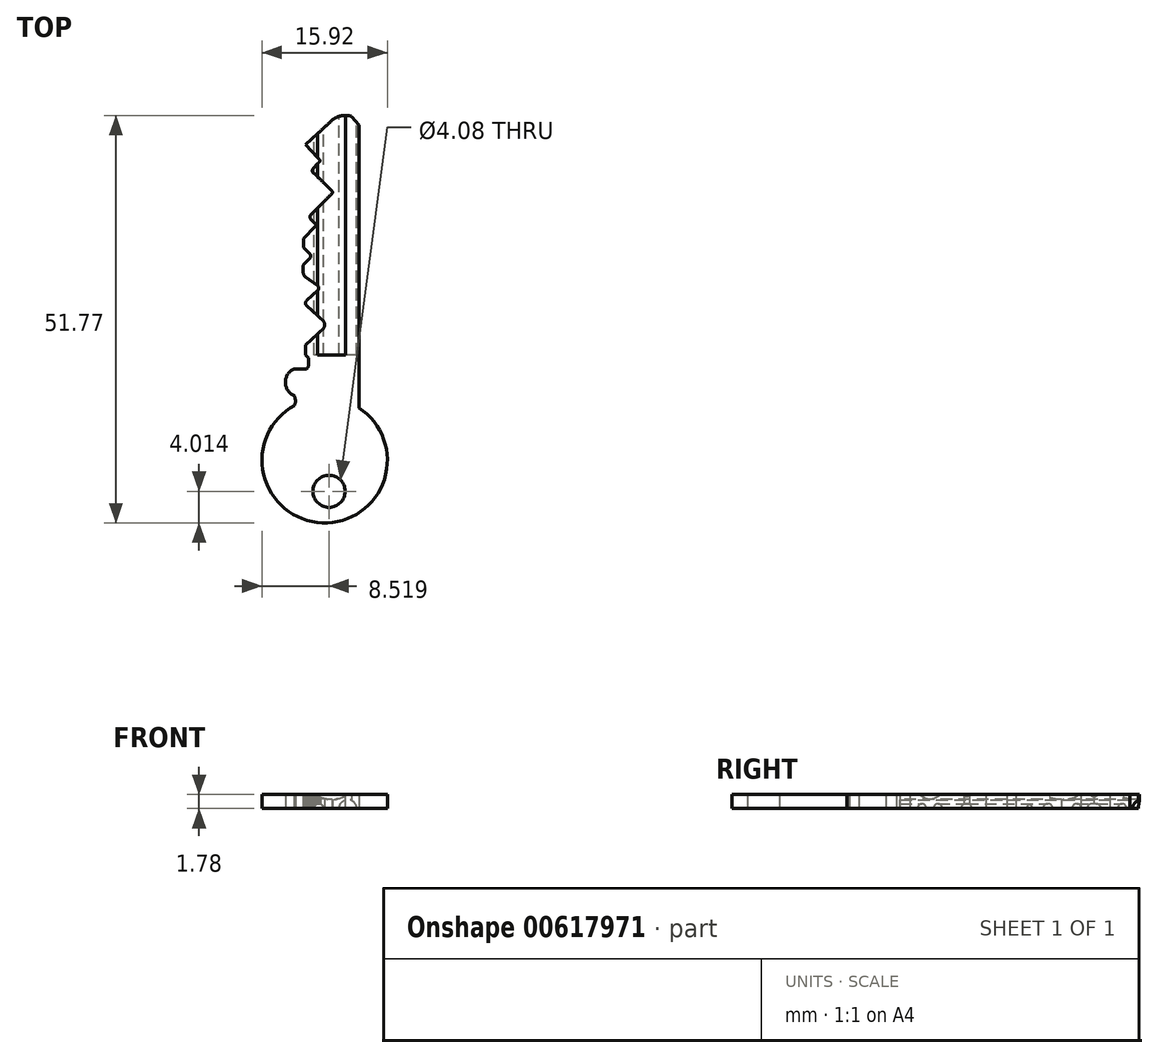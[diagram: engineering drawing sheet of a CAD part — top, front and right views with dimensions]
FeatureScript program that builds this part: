
annotation { "Feature Type Name" : "Feature", "Feature Type Description" : "" }
export const myFeature = defineFeature(function(context is Context, id is Id, definition is map)
    precondition{}
    {
        {
            var Q0;
            Q0=qCreatedBy(makeId("Top.planeOp"),FACE);
            var sketch = newSketch(context, id + "F0", { "sketchPlane" : qUnion([Q0])});
            skLineSegment(sketch, "E0", {"start": v(-2.25, 0) * mm, "end": v(-2.25, 27.94) * mm});
            skLineSegment(sketch, "E1", {"start": v(-2.25, 27.94) * mm, "end": v(-3.17, 29) * mm});
            skArc(sketch, "E2", {"start": v(-3.17, 29) * mm, "mid": v(-4.52, 29.1) * mm, "end": v(-5.72, 28.47) * mm});
            skPoint(sketch, "E2.endSnap0", {"position": v(-2.7, 28.47) * mm});
            skLineSegment(sketch, "E3", {"start": v(-5.72, 28.47) * mm, "end": v(-9.02, 25.42) * mm});
            skLineSegment(sketch, "E4", {"start": v(-9.02, 25.42) * mm, "end": v(-7.14, 23.39) * mm});
            skLineSegment(sketch, "E5", {"start": v(-7.14, 23.39) * mm, "end": v(-8.07, 22.39) * mm});
            skArc(sketch, "E6", {"start": v(-8.07, 22.39) * mm, "mid": v(-8.17, 22.02) * mm, "end": v(-7.92, 21.74) * mm});
            skLineSegment(sketch, "E7", {"start": v(-7.92, 21.74) * mm, "end": v(-5.67, 19.53) * mm});
            skArc(sketch, "E8", {"start": v(-5.67, 19.24) * mm, "mid": v(-5.6, 19.38) * mm, "end": v(-5.67, 19.53) * mm});
            skLineSegment(sketch, "E9", {"start": v(-5.67, 19.24) * mm, "end": v(-8.39, 16.47) * mm});
            skArc(sketch, "E10", {"start": v(-8.39, 16.47) * mm, "mid": v(-8.49, 16.23) * mm, "end": v(-8.39, 15.98) * mm});
            skLineSegment(sketch, "E11", {"start": v(-8.39, 15.98) * mm, "end": v(-7.8, 15.38) * mm});
            skArc(sketch, "E12", {"start": v(-7.8, 15) * mm, "mid": v(-7.72, 15.19) * mm, "end": v(-7.8, 15.38) * mm});
            skLineSegment(sketch, "E13", {"start": v(-7.8, 15) * mm, "end": v(-9.3, 13.47) * mm});
            skLineSegment(sketch, "E14", {"start": v(-9.3, 13.47) * mm, "end": v(-9.3, 12.33) * mm});
            skLineSegment(sketch, "E15", {"start": v(-9.3, 12.33) * mm, "end": v(-8.48, 11.53) * mm});
            skArc(sketch, "E16", {"start": v(-8.48, 10.99) * mm, "mid": v(-8.37, 11.26) * mm, "end": v(-8.48, 11.53) * mm});
            skLineSegment(sketch, "E17", {"start": v(-8.48, 10.99) * mm, "end": v(-9.19, 10.3) * mm});
            skArc(sketch, "E18", {"start": v(-9.19, 10.3) * mm, "mid": v(-9.36, 9.98) * mm, "end": v(-9.33, 9.63) * mm});
            skLineSegment(sketch, "E19", {"start": v(-9.33, 9.63) * mm, "end": v(-9.33, 9.19) * mm});
            skArc(sketch, "E20", {"start": v(-9.33, 9.19) * mm, "mid": v(-9.25, 8.86) * mm, "end": v(-9.02, 8.6) * mm});
            skLineSegment(sketch, "E21", {"start": v(-9.02, 8.6) * mm, "end": v(-7.53, 7.53) * mm});
            skArc(sketch, "E22", {"start": v(-7.53, 6.87) * mm, "mid": v(-7.35, 7.2) * mm, "end": v(-7.53, 7.53) * mm});
            skLineSegment(sketch, "E23", {"start": v(-7.53, 6.87) * mm, "end": v(-8.87, 5.67) * mm});
            skArc(sketch, "E24", {"start": v(-8.87, 5.67) * mm, "mid": v(-9.04, 5.3) * mm, "end": v(-8.87, 4.92) * mm});
            skLineSegment(sketch, "E25", {"start": v(-8.87, 4.92) * mm, "end": v(-6.89, 3.14) * mm});
            skArc(sketch, "E26", {"start": v(-6.89, 1.94) * mm, "mid": v(-6.62, 2.54) * mm, "end": v(-6.89, 3.14) * mm});
            skLineSegment(sketch, "E27", {"start": v(-6.89, 1.94) * mm, "end": v(-8.9, 0.15) * mm});
            skLineSegment(sketch, "E28", {"start": v(-8.9, 0.15) * mm, "end": v(-9.05, 0) * mm});
            skLineSegment(sketch, "E29", {"start": v(-9.05, 0) * mm, "end": v(-9.05, -1.3) * mm});
            skLineSegment(sketch, "E30", {"start": v(-9.05, -1.3) * mm, "end": v(-8.68, -1.71) * mm});
            skLineSegment(sketch, "E31", {"start": v(-8.68, -1.71) * mm, "end": v(-8.68, -2.67) * mm});
            skLineSegment(sketch, "E32", {"start": v(-2.25, 0) * mm, "end": v(-2.25, -2.91) * mm});
            skArc(sketch, "E33", {"start": v(-8.9, -3.06) * mm, "mid": v(-8.74, -2.9) * mm, "end": v(-8.68, -2.67) * mm});
            skLineSegment(sketch, "E34", {"start": v(-8.9, -3.06) * mm, "end": v(-10.5, -3.06) * mm});
            skArc(sketch, "E35", {"start": v(-10.5, -3.06) * mm, "mid": v(-11.6, -4.76) * mm, "end": v(-10.5, -6.46) * mm});
            skArc(sketch, "E36", {"start": v(-10.43, -7.69) * mm, "mid": v(-10.32, -7.07) * mm, "end": v(-10.5, -6.46) * mm});
            skLineSegment(sketch, "E37", {"start": v(-2.25, -2.91) * mm, "end": v(-2.25, -8) * mm});
            skArc(sketch, "E38", {"start": v(-10.43, -7.69) * mm, "mid": v(-6.92, -22.62) * mm, "end": v(-2.25, -8) * mm});
            skCircle(sketch, "E39", {"center": v(-6.05, -18.62) * mm, "radius": 2.04 * mm});
            skPoint(sketch, "E40.orphan", {"position": v(-10.5, -7.82) * mm});
            skPoint(sketch, "E41.end.orphan", {"position": v(-11.92, -8) * mm});
            skPoint(sketch, "E42.orphan", {"position": v(-7.08, -8) * mm});
            skPoint(sketch, "E43.end.orphan", {"position": v(-6.05, -16.58) * mm});
            skSolve(sketch);
        }
        {
            var Q0;
            Q0 = qSketchRegion(id + "F0", true);
            extrude(context, id + "F1", {"entities" : qUnion([Q0]), "depth" : 1.78 * mm, "offsetDistance" : 25.4 * mm});
        }
        {
            var Q0;
            Q0=qCreatedBy(makeId("Front.planeOp"),FACE);
            cPlane(context, id + "F2", {"entities" : qUnion([Q0]), "cplaneType" : CPlaneType.OFFSET, "offset" : 29.2 * mm, "oppositeDirection" : true, "width" : 152.4 * mm, "height" : 152.4 * mm});
        }
        {
            var Q0;
            Q0=qCreatedBy(id+"F2.planeOp",FACE);
            var sketch = newSketch(context, id + "F3", { "sketchPlane" : qUnion([Q0])});
            skLineSegment(sketch, "E44.0", {"start": v(-3.93, 1.78) * mm, "end": v(-5.72, 1.78) * mm});
            skLineSegment(sketch, "E45.0", {"start": v(-5.72, 1.78) * mm, "end": v(-7.5, 1.78) * mm});
            skLineSegment(sketch, "E46.0", {"start": v(-6.75, 0) * mm, "end": v(-7.96, 0) * mm});
            skLineSegment(sketch, "E47.0", {"start": v(-3.17, 0) * mm, "end": v(-4.78, 0) * mm});
            skPoint(sketch, "E48.0", {"position": v(-7.35, 0) * mm});
            skArc(sketch, "E49", {"start": v(-7.96, 0) * mm, "mid": v(-7.35, 0.6) * mm, "end": v(-6.75, 0) * mm});
            skLineSegment(sketch, "E50.0", {"start": v(-2.54, 0) * mm, "end": v(-3.17, 0) * mm});
            skArc(sketch, "E51", {"start": v(-4.78, 0) * mm, "mid": v(-3.66, 1.12) * mm, "end": v(-2.54, 0) * mm});
            skLineSegment(sketch, "E52", {"start": v(-2.54, 0) * mm, "end": v(-4.78, 0) * mm});
            skEllipticalArc(sketch, "E53", {});
            skLineSegment(sketch, "E54", {"start": v(-3.93, 1.78) * mm, "end": v(-7.5, 1.78) * mm});
            skPoint(sketch, "E55.orphan", {"position": v(-10.5, 1.78) * mm});
            skPoint(sketch, "E56.orphan", {"position": v(-10.5, 0) * mm});
            skPoint(sketch, "E57.0.end.orphan", {"position": v(-3.17, 1.78) * mm});
            skPoint(sketch, "E58.0.start.orphan", {"position": v(-2.25, 1.78) * mm});
            skPoint(sketch, "E59.orphan", {"position": v(-2.25, 0) * mm});
            skPoint(sketch, "E60.orphan", {"position": v(-5.72, 0) * mm});
            skPoint(sketch, "E61.trimOffspring.end.orphan", {"position": v(-9.02, 0) * mm});
            skPoint(sketch, "E61.trimOffspring.start.orphan", {"position": v(-8.9, 0) * mm});
            skPoint(sketch, "E62.trimOffspring.end.orphan", {"position": v(-9.02, 1.78) * mm});
            skPoint(sketch, "E62.trimOffspring.start.orphan", {"position": v(-8.9, 1.78) * mm});
            const initialGuessF3  = {"E53": [-0.005718471948057415, 0.001778, -1, 0, 0.001789613161236046, 0.0006257904186615492, 0, 3.141592653589793]};
            skSetInitialGuess(sketch, initialGuessF3);
            skSolve(sketch);
        }
        {
            var Q0;
            Q0 = qSketchRegion(id + "F3", true);
            extrude(context, id + "F4", {"entities" : qUnion([Q0]), "operationType" : NewBodyOperationType.REMOVE, "depth" : 30.48 * mm, "offsetDistance" : 25.4 * mm});
        }
    });
